# Revit family: 15-42-0035-DN040-400
name_source: partatom
category: Pipe Accessories
units: mm (PartAtom-declared; Revit-internal decimal feet)

## family parameters
Always vertical = No
Cut with Voids When Loaded = No
Part Type = Valve - Breaks Into
Round Connector Dimension = Use Diameter
Shared = No
Work Plane-Based = No

## types (12) — shared parameters
Body_Wallthickness = 15 mm  [stored 0.0492126 ft]
DN 050 = Yes
DN040_PN10/16 = 15-040-40-016
DN050_PN10/16 = 15-050-40-016
DN065_PN10/16 = 15-065-42-016
DN080_PN10/16 = 15-080-42-01464099
DN100_PN10/16 = 15-100-42-01464099
DN125_PN10/16 = 15-125-42-01464099
DN150_PN10/16 = 15-150-42-01464099
DN200_PN10 = 15-200-42-00464099
DN200_PN16 = 15-200-42-01464099
DN250_PN10 = 15-250-42-006
DN250_PN16 = 15-250-42-016
DN300_PN10 = 15-300-42-006
DN300_PN16 = 15-300-42-016
DN350_PN10 = 15-350-40-006
DN350_PN16 = 15-350-40-016
DN400_PN10 = 15-400-40-006
Ftc = 4 mm  [stored 0.0131234 ft]
Name_Height_reference = 10 mm  [stored 0.0328084 ft]
Rib_Thickness = 18 mm  [stored 0.0590551 ft]
Search_table = 15-42-0035-DN040-400
zero-valued in all types: Bottom_Reference

## per-type parameters (varying)
- DN 040: At=46 mm  [stored 0.150919 ft]; Body_Height=101 mm; Body_depth=92 mm; Body_width=74 mm; Bonnet_Flange_Depth=118 mm; Bonnet_Flange_Width=68 mm; Bonnet_Flange_cut=8 mm  [stored 0.0262467 ft]; Bonnet_Flange_thickness=15 mm  [stored 0.0492126 ft]; Bonnet_Height=38 mm  [stored 0.124672 ft]; Bonnet_Reference_height=91 mm; Bonnet_Thickness=75 mm; Bt=75 mm; Bt_2=68 mm; CL _Thickness=26 mm; CL_Height=51 mm; Cut_Reference=280 mm; D=63 mm; D1=10 mm  [stored 0.0328084 ft]; D2=39 mm  [stored 0.127953 ft]; DN 040=Yes; DN 065=Yes; DN 080=Yes; DN 100=Yes; DN 125=Yes; DN 150=Yes; DN 200=Yes; DN 250=Yes; DN 300=Yes; DN 350=Yes; DN 400=Yes; DN400_PN16=15-400-40-016; Description_=AVK_GATE_VALVE,FLANGED; E=14 mm  [stored 0.0459318 ft]; F1=16 mm  [stored 0.0524934 ft]; Fillet_Thickness=6 mm  [stored 0.019685 ft]; Flange_OR=75 mm; Flange_Thickness=19 mm  [stored 0.062336 ft]; Flange_Thickness_cut=28 mm  [stored 0.0918635 ft]; Ftc_reference_height=75 mm; H=241 mm; H1=202 mm; H3=277 mm; Horizontal_Flange_width=72 mm; ID (Radius)=20 mm  [stored 0.0656168 ft]; L=140 mm; L_Dia=40 mm  [stored 0.131234 ft]; Name_Reference=67 mm; Name_Width=37 mm  [stored 0.121391 ft]; Neck_H=37 mm  [stored 0.121391 ft]; Neck_T=24 mm  [stored 0.0787402 ft]; Neck_T2=22 mm  [stored 0.0721785 ft]; Nominal Diameter (DN)=40 mm  [stored 0.131234 ft]; R1tv=750 mm; R2f=15 mm  [stored 0.0492126 ft]; RF_Dia=42 mm  [stored 0.137795 ft]; Rf=120 mm; Rib_Height_Reference_1=120 mm; Rib_Height_Reference_2=110 mm; Rib_Height_Reference_3=100 mm; Rib_Height_Reference_4=40 mm  [stored 0.131234 ft]; Rib_Width_1=37 mm  [stored 0.121391 ft]; Rib_Width_2=37 mm  [stored 0.121391 ft]; Rib_Width_3=37 mm  [stored 0.121391 ft]; Rib_depth_1=37 mm  [stored 0.121391 ft]; Rib_depth_2=37 mm  [stored 0.121391 ft]; Rib_depth_3=37 mm  [stored 0.121391 ft]; Rt=250 mm; URL product pages=https://www.avkvalves.com
- DN 050: At=45 mm  [stored 0.147638 ft]; Body_Height=101 mm; Body_depth=90 mm; Body_width=72 mm; Bonnet_Flange_Depth=118 mm; Bonnet_Flange_Width=82 mm; Bonnet_Flange_cut=8 mm  [stored 0.0262467 ft]; Bonnet_Flange_thickness=15 mm  [stored 0.0492126 ft]; Bonnet_Height=41 mm; Bonnet_Reference_height=91 mm; Bonnet_Thickness=73 mm; Bt=73 mm; Bt_2=66 mm; CL _Thickness=25 mm  [stored 0.082021 ft]; CL_Height=50 mm; Cut_Reference=300 mm; D=63 mm; D1=10 mm  [stored 0.0328084 ft]; D2=39 mm  [stored 0.127953 ft]; DN 040=No; DN 065=No; DN 080=No; DN 100=No; DN 125=No; DN 150=No; DN 200=No; DN 250=No; DN 300=No; DN 350=No; DN 400=No; DN400_PN16=15-400-40-016; Description_=AVK_GATE_VALVE,FLANGED; E=11 mm  [stored 0.0360892 ft]; F1=16 mm  [stored 0.0524934 ft]; Fillet_Thickness=6 mm  [stored 0.019685 ft]; Flange_OR=83 mm; Flange_Thickness=19 mm  [stored 0.062336 ft]; Flange_Thickness_cut=29 mm  [stored 0.0951444 ft]; Ftc_reference_height=83 mm; H=241 mm; H1=202 mm; H3=324 mm; Horizontal_Flange_width=166 mm; ID (Radius)=25 mm  [stored 0.082021 ft]; L=150 mm; L_Dia=50 mm; Name_Reference=71 mm; Name_Width=36 mm  [stored 0.11811 ft]; Neck_H=41 mm; Neck_T=23 mm  [stored 0.0754593 ft]; Neck_T2=21 mm; Nominal Diameter (DN)=50 mm; R1tv=825 mm; R2f=15 mm  [stored 0.0492126 ft]; RF_Dia=50 mm; Rf=277 mm; Rib_Height_Reference_1=120 mm; Rib_Height_Reference_2=110 mm; Rib_Height_Reference_3=100 mm; Rib_Height_Reference_4=60 mm; Rib_Width_1=36 mm  [stored 0.11811 ft]; Rib_Width_2=36 mm  [stored 0.11811 ft]; Rib_Width_3=36 mm  [stored 0.11811 ft]; Rib_depth_1=36 mm  [stored 0.11811 ft]; Rib_depth_2=36 mm  [stored 0.11811 ft]; Rib_depth_3=36 mm  [stored 0.11811 ft]; Rt=275 mm; URL product pages=https://www.avkvalves.com
- DN 065: At=54 mm; Body_Height=115 mm; Body_depth=107 mm; Body_width=72 mm; Bonnet_Flange_Depth=135 mm; Bonnet_Flange_Width=65 mm; Bonnet_Flange_cut=8 mm  [stored 0.0262467 ft]; Bonnet_Flange_thickness=15 mm  [stored 0.0492126 ft]; Bonnet_Height=47 mm  [stored 0.154199 ft]; Bonnet_Reference_height=105 mm; Bonnet_Thickness=73 mm; Bt=73 mm; Bt_2=66 mm; CL _Thickness=25 mm  [stored 0.082021 ft]; CL_Height=59 mm; Cut_Reference=340 mm; D=63 mm; D1=10 mm  [stored 0.0328084 ft]; D2=51 mm; DN 040=Yes; DN 065=Yes; DN 080=Yes; DN 100=Yes; DN 125=Yes; DN 150=Yes; DN 200=Yes; DN 250=Yes; DN 300=Yes; DN 350=Yes; DN 400=Yes; DN400_PN16=15-400-40-016; Description_=AVK_GATE-VALVE,FLANGED; E=11 mm  [stored 0.0360892 ft]; F1=20 mm  [stored 0.0656168 ft]; Fillet_Thickness=6 mm  [stored 0.019685 ft]; Flange_OR=93 mm; Flange_Thickness=19 mm  [stored 0.062336 ft]; Flange_Thickness_cut=30 mm  [stored 0.0984252 ft]; Ftc_reference_height=93 mm; H=278 mm; H1=227 mm; H3=371 mm; Horizontal_Flange_width=186 mm; ID (Radius)=33 mm  [stored 0.108268 ft]; L=170 mm; L_Dia=65 mm; Name_Reference=96 mm; Name_Width=36 mm  [stored 0.11811 ft]; Neck_H=43 mm; Neck_T=23 mm  [stored 0.0754593 ft]; Neck_T2=21 mm; Nominal Diameter (DN)=65 mm; R1tv=930 mm; R2f=15 mm  [stored 0.0492126 ft]; RF_Dia=59 mm; Rf=310 mm; Rib_Height_Reference_1=120 mm; Rib_Height_Reference_2=110 mm; Rib_Height_Reference_3=100 mm; Rib_Height_Reference_4=75 mm; Rib_Width_1=36 mm  [stored 0.11811 ft]; Rib_Width_2=36 mm  [stored 0.11811 ft]; Rib_Width_3=36 mm  [stored 0.11811 ft]; Rib_depth_1=36 mm  [stored 0.11811 ft]; Rib_depth_2=36 mm  [stored 0.11811 ft]; Rib_depth_3=36 mm  [stored 0.11811 ft]; Rt=310 mm; URL product pages=https://www.avkvalves.com
- DN 080: At=70 mm; Body_Height=108 mm; Body_depth=140 mm; Body_width=75 mm; Bonnet_Flange_Depth=171 mm; Bonnet_Flange_Width=76 mm; Bonnet_Flange_cut=8 mm  [stored 0.0262467 ft]; Bonnet_Flange_thickness=15 mm  [stored 0.0492126 ft]; Bonnet_Height=50 mm; Bonnet_Reference_height=98 mm; Bonnet_Thickness=77 mm; Bt=77 mm; Bt_2=69 mm; CL _Thickness=27 mm  [stored 0.0885827 ft]; CL_Height=75 mm; Cut_Reference=360 mm; D=63 mm; D1=10 mm  [stored 0.0328084 ft]; D2=37 mm  [stored 0.121391 ft]; DN 040=Yes; DN 065=Yes; DN 080=Yes; DN 100=Yes; DN 125=Yes; DN 150=Yes; DN 200=Yes; DN 250=Yes; DN 300=Yes; DN 350=Yes; DN 400=Yes; DN400_PN16=15-400-40-016; Description_=AVK_GATE_VALVE,FLANGED; E=15 mm  [stored 0.0492126 ft]; F1=20 mm  [stored 0.0656168 ft]; Fillet_Thickness=6 mm  [stored 0.019685 ft]; Flange_OR=100 mm; Flange_Thickness=19 mm  [stored 0.062336 ft]; Flange_Thickness_cut=30 mm  [stored 0.0984252 ft]; Ftc_reference_height=100 mm; H=284 mm; H1=247 mm; H3=384 mm; Horizontal_Flange_width=200 mm; ID (Radius)=40 mm  [stored 0.131234 ft]; L=180 mm; L_Dia=80 mm; Name_Reference=90 mm; Name_Width=38 mm  [stored 0.124672 ft]; Neck_H=49 mm; Neck_T=25 mm  [stored 0.082021 ft]; Neck_T2=23 mm  [stored 0.0754593 ft]; Nominal Diameter (DN)=80 mm; R1tv=1000 mm; R2f=15 mm  [stored 0.0492126 ft]; RF_Dia=66 mm; Rf=333 mm; Rib_Height_Reference_1=120 mm; Rib_Height_Reference_2=110 mm; Rib_Height_Reference_3=100 mm; Rib_Height_Reference_4=85 mm; Rib_Width_1=38 mm  [stored 0.124672 ft]; Rib_Width_2=38 mm  [stored 0.124672 ft]; Rib_Width_3=38 mm  [stored 0.124672 ft]; Rib_depth_1=38 mm  [stored 0.124672 ft]; Rib_depth_2=38 mm  [stored 0.124672 ft]; Rib_depth_3=38 mm  [stored 0.124672 ft]; Rt=333 mm; URL product pages=https://www.avkvalves.com
- DN 100: At=83 mm; Body_Height=122 mm; Body_depth=166 mm; Body_width=80 mm; Bonnet_Flange_Depth=192 mm; Bonnet_Flange_Width=81 mm; Bonnet_Flange_cut=8 mm  [stored 0.0262467 ft]; Bonnet_Flange_thickness=15 mm  [stored 0.0492126 ft]; Bonnet_Height=55 mm; Bonnet_Reference_height=112 mm; Bonnet_Thickness=82 mm; Bt=82 mm; Bt_2=74 mm; CL _Thickness=29 mm  [stored 0.0951444 ft]; CL_Height=88 mm; Cut_Reference=380 mm; D=63 mm; D1=10 mm  [stored 0.0328084 ft]; D2=41 mm; DN 040=Yes; DN 065=Yes; DN 080=Yes; DN 100=Yes; DN 125=Yes; DN 150=Yes; DN 200=Yes; DN 250=Yes; DN 300=Yes; DN 350=Yes; DN 400=Yes; DN400_PN16=15-400-40-016; Description_=AVK_GATE_VALVE,FLANGED; E=15 mm  [stored 0.0492126 ft]; F1=22 mm  [stored 0.0721785 ft]; Fillet_Thickness=6 mm  [stored 0.019685 ft]; Flange_OR=110 mm; Flange_Thickness=19 mm  [stored 0.062336 ft]; Flange_Thickness_cut=30 mm  [stored 0.0984252 ft]; Ftc_reference_height=110 mm; H=311 mm; H1=270 mm; H3=421 mm; Horizontal_Flange_width=220 mm; ID (Radius)=50 mm; L=190 mm; L_Dia=100 mm; Name_Reference=101 mm; Name_Width=40 mm  [stored 0.131234 ft]; Neck_H=45 mm  [stored 0.147638 ft]; Neck_T=27 mm  [stored 0.0885827 ft]; Neck_T2=25 mm  [stored 0.082021 ft]; Nominal Diameter (DN)=100 mm; R1tv=1100 mm; R2f=15 mm  [stored 0.0492126 ft]; RF_Dia=78 mm; Rf=367 mm; Rib_Height_Reference_1=120 mm; Rib_Height_Reference_2=110 mm; Rib_Height_Reference_3=100 mm; Rib_Height_Reference_4=90 mm; Rib_Width_1=40 mm  [stored 0.131234 ft]; Rib_Width_2=40 mm  [stored 0.131234 ft]; Rib_Width_3=40 mm  [stored 0.131234 ft]; Rib_depth_1=40 mm  [stored 0.131234 ft]; Rib_depth_2=40 mm  [stored 0.131234 ft]; Rib_depth_3=40 mm  [stored 0.131234 ft]; Rt=367 mm; URL product pages=https://www.avkvalves.com
- DN 150: At=121 mm; Body_Height=172 mm; Body_depth=242 mm; Body_width=95 mm; Bonnet_Flange_Depth=272 mm; Bonnet_Flange_Width=116 mm; Bonnet_Flange_cut=8 mm  [stored 0.0262467 ft]; Bonnet_Flange_thickness=15 mm  [stored 0.0492126 ft]; Bonnet_Height=71 mm; Bonnet_Reference_height=162 mm; Bonnet_Thickness=97 mm; Bt=97 mm; Bt_2=89 mm; CL _Thickness=34 mm  [stored 0.111549 ft]; CL_Height=126 mm; Cut_Reference=420 mm; D=63 mm; D1=10 mm  [stored 0.0328084 ft]; D2=43 mm; DN 040=Yes; DN 065=Yes; DN 080=Yes; DN 100=Yes; DN 125=Yes; DN 150=Yes; DN 200=Yes; DN 250=Yes; DN 300=Yes; DN 350=Yes; DN 400=Yes; DN400_PN16=15-400-40-016
15-400-40-016
15-400-40-016
15-400-40-016
15-400-40-016; Description_=AVK_GATE_VALVE,FLANGED; E=15 mm  [stored 0.0492126 ft]; F1=22 mm  [stored 0.0721785 ft]; Fillet_Thickness=12 mm  [stored 0.0393701 ft]; Flange_OR=142 mm; Flange_Thickness=19 mm  [stored 0.062336 ft]; Flange_Thickness_cut=34 mm  [stored 0.111549 ft]; Ftc_reference_height=142 mm; H=408 mm; H1=365 mm; H3=550 mm; Horizontal_Flange_width=284 mm; ID (Radius)=75 mm; L=210 mm; L_Dia=150 mm; Name_Reference=143 mm; Name_Width=48 mm; Neck_H=52 mm; Neck_T=32 mm  [stored 0.104987 ft]; Neck_T2=30 mm  [stored 0.0984252 ft]; Nominal Diameter (DN)=150 mm; R1tv=1420 mm; R2f=30 mm  [stored 0.0984252 ft]; RF_Dia=106 mm; Rf=473 mm; Rib_Height_Reference_1=120 mm; Rib_Height_Reference_2=110 mm; Rib_Height_Reference_3=100 mm; Rib_Height_Reference_4=150 mm; Rib_Width_1=48 mm; Rib_Width_2=48 mm; Rib_Width_3=48 mm; Rib_depth_1=48 mm; Rib_depth_2=48 mm; Rib_depth_3=48 mm; Rt=473 mm; URL product pages=https://www.avkvalves.com
- DN 200: At=147 mm; Body_Height=220 mm; Body_depth=294 mm; Body_width=108 mm; Bonnet_Flange_Depth=332 mm; Bonnet_Flange_Width=132 mm; Bonnet_Flange_cut=13 mm; Bonnet_Flange_thickness=25 mm  [stored 0.082021 ft]; Bonnet_Height=85 mm; Bonnet_Reference_height=210 mm; Bonnet_Thickness=110 mm; Bt=110 mm; Bt_2=102 mm; CL _Thickness=34 mm  [stored 0.111549 ft]; CL_Height=152 mm; Cut_Reference=460 mm; D=63 mm; D1=10 mm  [stored 0.0328084 ft]; D2=51 mm; DN 040=Yes; DN 065=Yes; DN 080=Yes; DN 100=Yes; DN 125=Yes; DN 150=Yes; DN 200=Yes; DN 250=Yes; DN 300=Yes; DN 350=Yes; DN 400=Yes; DN400_PN16=15-400-40-016; Description_=AVK_GATE_VALVE,FLANGED; E=15 mm  [stored 0.0492126 ft]; F1=28 mm  [stored 0.0918635 ft]; Fillet_Thickness=24 mm  [stored 0.0787402 ft]; Flange_OR=170 mm; Flange_Thickness=20 mm  [stored 0.0656168 ft]; Flange_Thickness_cut=35 mm  [stored 0.114829 ft]; Ftc_reference_height=170 mm; H=507 mm; H1=456 mm; H3=677 mm; Horizontal_Flange_width=340 mm; ID (Radius)=100 mm; L=230 mm; L_Dia=200 mm; Name_Reference=183 mm; Name_Width=54 mm; Neck_H=69 mm; Neck_T=32 mm  [stored 0.104987 ft]; Neck_T2=30 mm  [stored 0.0984252 ft]; Nominal Diameter (DN)=200 mm; R1tv=1700 mm; R2f=60 mm; RF_Dia=133 mm; Rf=567 mm; Rib_Height_Reference_1=120 mm; Rib_Height_Reference_2=110 mm; Rib_Height_Reference_3=100 mm; Rib_Height_Reference_4=180 mm; Rib_Width_1=54 mm; Rib_Width_2=54 mm; Rib_Width_3=54 mm; Rib_depth_1=54 mm; Rib_depth_2=54 mm; Rib_depth_3=54 mm; Rt=567 mm; URL product pages=https://www.avkvalves.com
https://www.avkvalves.com
- DN 250: At=171 mm; Body_Height=305 mm; Body_depth=342 mm; Body_width=124 mm; Bonnet_Flange_Depth=372 mm; Bonnet_Flange_Width=158 mm; Bonnet_Flange_cut=13 mm; Bonnet_Flange_thickness=25 mm  [stored 0.082021 ft]; Bonnet_Height=100 mm; Bonnet_Reference_height=295 mm; Bonnet_Thickness=126 mm; Bt=126 mm; Bt_2=118 mm; CL _Thickness=42 mm  [stored 0.137795 ft]; CL_Height=176 mm; Cut_Reference=500 mm; D=88 mm; D1=15 mm  [stored 0.0492126 ft]; D2=62 mm; DN 040=Yes; DN 065=Yes; DN 080=Yes; DN 100=Yes; DN 125=Yes; DN 150=Yes; DN 200=Yes; DN 250=Yes; DN 300=Yes; DN 350=Yes; DN 400=Yes; DN400_PN16=15-400-40-016; Description_=AVK_GATE_VALVE,FLANGED; E=13 mm; F1=27 mm  [stored 0.0885827 ft]; Fillet_Thickness=24 mm  [stored 0.0787402 ft]; Flange_OR=200 mm; Flange_Thickness=22 mm  [stored 0.0721785 ft]; Flange_Thickness_cut=38 mm  [stored 0.124672 ft]; Ftc_reference_height=200 mm; H=617 mm; H1=555 mm; H3=817 mm; Horizontal_Flange_width=400 mm; ID (Radius)=125 mm; L=250 mm; L_Dia=250 mm; Name_Reference=270 mm; Name_Width=62 mm; Neck_H=61 mm; Neck_T=40 mm  [stored 0.131234 ft]; Neck_T2=38 mm  [stored 0.124672 ft]; Nominal Diameter (DN)=250 mm; R1tv=2000 mm; R2f=60 mm; RF_Dia=160 mm; Rf=667 mm; Rib_Height_Reference_1=90 mm; Rib_Height_Reference_2=110 mm; Rib_Height_Reference_3=100 mm; Rib_Height_Reference_4=200 mm; Rib_Width_1=140 mm; Rib_Width_2=140 mm; Rib_Width_3=62 mm; Rib_depth_1=372 mm; Rib_depth_2=62 mm; Rib_depth_3=62 mm; Rt=667 mm; URL product pages=https://www.avkvalves.com
- DN 300: At=209 mm; Body_Height=370 mm; Body_depth=418 mm; Body_width=157 mm; Bonnet_Flange_Depth=432 mm; Bonnet_Flange_Width=206 mm; Bonnet_Flange_cut=18 mm  [stored 0.0590551 ft]; Bonnet_Flange_thickness=35 mm  [stored 0.114829 ft]; Bonnet_Height=114 mm; Bonnet_Reference_height=360 mm; Bonnet_Thickness=160 mm; Bt=160 mm; Bt_2=151 mm; CL _Thickness=59 mm; CL_Height=214 mm; Cut_Reference=540 mm; D=88 mm; D1=15 mm  [stored 0.0492126 ft]; D2=61 mm; DN 040=Yes; DN 065=Yes; DN 080=Yes; DN 100=Yes; DN 125=Yes; DN 150=Yes; DN 200=Yes; DN 250=Yes; DN 300=Yes; DN 350=Yes; DN 400=Yes; DN400_PN16=15-400-40-016; Description_=AVK_GATE_VALVE,FLANGED; E=13 mm; F1=27 mm  [stored 0.0885827 ft]; Fillet_Thickness=24 mm  [stored 0.0787402 ft]; Flange_OR=228 mm; Flange_Thickness=25 mm  [stored 0.082021 ft]; Flange_Thickness_cut=39 mm  [stored 0.127953 ft]; Ftc_reference_height=228 mm; H=691 mm; H1=630 mm; H3=919 mm; Horizontal_Flange_width=456 mm; ID (Radius)=150 mm; L=270 mm; L_Dia=300 mm; Name_Reference=250 mm; Name_Width=79 mm; Neck_H=33 mm  [stored 0.108268 ft]; Neck_T=57 mm; Neck_T2=55 mm; Nominal Diameter (DN)=300 mm; R1tv=2280 mm; R2f=60 mm; RF_Dia=185 mm; Rf=760 mm; Rib_Height_Reference_1=178 mm; Rib_Height_Reference_2=285 mm; Rib_Height_Reference_3=150 mm; Rib_Height_Reference_4=300 mm; Rib_Width_1=168 mm; Rib_Width_2=168 mm; Rib_Width_3=79 mm; Rib_depth_1=432 mm; Rib_depth_2=432 mm; Rib_depth_3=79 mm; Rt=760 mm; URL product pages=https://www.avkvalves.com
- DN 350: At=250 mm; Body_Height=485 mm; Body_depth=500 mm; Body_width=170 mm; Bonnet_Flange_Depth=554 mm; Bonnet_Flange_Width=180 mm; Bonnet_Flange_cut=18 mm  [stored 0.0590551 ft]; Bonnet_Flange_thickness=35 mm  [stored 0.114829 ft]; Bonnet_Height=130 mm; Bonnet_Reference_height=475 mm; Bonnet_Thickness=173 mm; Bt=173 mm; Bt_2=164 mm; CL _Thickness=65 mm; CL_Height=255 mm; Cut_Reference=580 mm; D=110 mm; D1=15 mm  [stored 0.0492126 ft]; D2=107 mm; DN 040=Yes; DN 065=Yes; DN 080=Yes; DN 100=Yes; DN 125=Yes; DN 150=Yes; DN 200=Yes; DN 250=Yes; DN 300=Yes; DN 350=Yes; DN 400=Yes; DN400_PN16=15-400-40-016; Description_=AVK_GATE_VALVE,FLANGED; E=28 mm  [stored 0.0918635 ft]; F1=37 mm  [stored 0.121391 ft]; Fillet_Thickness=24 mm  [stored 0.0787402 ft]; Flange_OR=260 mm; Flange_Thickness=27 mm  [stored 0.0885827 ft]; Flange_Thickness_cut=43 mm; Ftc_reference_height=260 mm; H=907 mm; H1=800 mm; H3=1221 mm; Horizontal_Flange_width=628 mm; ID (Radius)=175 mm; L=290 mm; L_Dia=350 mm; Name_Reference=404 mm; Name_Width=85 mm; Neck_H=32 mm  [stored 0.104987 ft]; Neck_T=63 mm; Neck_T2=61 mm; Nominal Diameter (DN)=350 mm; R1tv=2600 mm; R2f=60 mm; RF_Dia=215 mm; Rf=1047 mm; Rib_Height_Reference_1=70 mm; Rib_Height_Reference_2=185 mm; Rib_Height_Reference_3=305 mm; Rib_Height_Reference_4=410 mm; Rib_Width_1=190 mm; Rib_Width_2=190 mm; Rib_Width_3=190 mm; Rib_depth_1=560 mm; Rib_depth_2=560 mm; Rib_depth_3=560 mm; Rt=867 mm; URL product pages=https://www.avkvalves.com
- DN 400: At=260 mm; Body_Height=512 mm; Body_depth=520 mm; Body_width=200 mm; Bonnet_Flange_Depth=554 mm; Bonnet_Flange_Width=194 mm; Bonnet_Flange_cut=35 mm  [stored 0.114829 ft]; Bonnet_Flange_thickness=70 mm; Bonnet_Height=145 mm; Bonnet_Reference_height=502 mm; Bonnet_Thickness=204 mm; Bt=204 mm; Bt_2=194 mm; CL _Thickness=76 mm; CL_Height=265 mm; Cut_Reference=620 mm; D=110 mm; D1=15 mm  [stored 0.0492126 ft]; D2=91 mm; DN 040=Yes; DN 065=Yes; DN 080=Yes; DN 100=Yes; DN 125=Yes; DN 150=Yes; DN 200=Yes; DN 250=Yes; DN 300=Yes; DN 350=Yes; DN 400=Yes; DN400_PN16=15-400-40-016; Description_=AVK_GATE_VALVE,FLANGED; E=28 mm  [stored 0.0918635 ft]; F1=37 mm  [stored 0.121391 ft]; Fillet_Thickness=32 mm  [stored 0.104987 ft]; Flange_OR=290 mm; Flange_Thickness=28 mm  [stored 0.0918635 ft]; Flange_Thickness_cut=45 mm  [stored 0.147638 ft]; Ftc_reference_height=290 mm; H=951 mm; H1=860 mm; H3=1239 mm; Horizontal_Flange_width=576 mm; ID (Radius)=200 mm; L=310 mm; L_Dia=400 mm; Name_Reference=426 mm; Name_Width=100 mm; Neck_H=55 mm; Neck_T=74 mm; Neck_T2=72 mm; Nominal Diameter (DN)=400 mm; R1tv=2900 mm; R2f=80 mm; RF_Dia=240 mm; Rf=960 mm; Rib_Height_Reference_1=81 mm; Rib_Height_Reference_2=210 mm; Rib_Height_Reference_3=330 mm; Rib_Height_Reference_4=440 mm; Rib_Width_1=248 mm; Rib_Width_2=248 mm; Rib_Width_3=248 mm; Rib_depth_1=564 mm; Rib_depth_2=564 mm; Rib_depth_3=564 mm; Rt=967 mm; URL product pages=https://www.avkvalves.com
- DN 125: At=97 mm; Body_Height=137 mm; Body_depth=194 mm; Body_width=90 mm; Bonnet_Flange_Depth=220 mm; Bonnet_Flange_Width=83 mm; Bonnet_Flange_cut=8 mm  [stored 0.0262467 ft]; Bonnet_Flange_thickness=15 mm  [stored 0.0492126 ft]; Bonnet_Height=63 mm; Bonnet_Reference_height=127 mm; Bonnet_Thickness=92 mm; Bt=92 mm; Bt_2=84 mm; CL _Thickness=34 mm  [stored 0.111549 ft]; CL_Height=102 mm; Cut_Reference=400 mm; D=63 mm; D1=10 mm  [stored 0.0328084 ft]; D2=41 mm; DN 040=Yes; DN 065=Yes; DN 080=Yes; DN 100=Yes; DN 125=Yes; DN 150=Yes; DN 200=Yes; DN 250=Yes; DN 300=Yes; DN 350=Yes; DN 400=Yes; DN400_PN16=15-400-40-016; Description_=AVK_GATE_VALVE,FLANGED; E=15 mm  [stored 0.0492126 ft]; F1=22 mm  [stored 0.0721785 ft]; Fillet_Thickness=6 mm  [stored 0.019685 ft]; Flange_OR=125 mm; Flange_Thickness=19 mm  [stored 0.062336 ft]; Flange_Thickness_cut=31 mm; Ftc_reference_height=125 mm; H=352 mm; H1=311 mm; H3=477 mm; Horizontal_Flange_width=250 mm; ID (Radius)=63 mm; L=200 mm; L_Dia=125 mm; Name_Reference=114 mm; Name_Width=45 mm  [stored 0.147638 ft]; Neck_H=57 mm; Neck_T=32 mm  [stored 0.104987 ft]; Neck_T2=30 mm  [stored 0.0984252 ft]; Nominal Diameter (DN)=125 mm; R1tv=1250 mm; R2f=15 mm  [stored 0.0492126 ft]; RF_Dia=92 mm; Rf=417 mm; Rib_Height_Reference_1=120 mm; Rib_Height_Reference_2=110 mm; Rib_Height_Reference_3=100 mm; Rib_Height_Reference_4=120 mm; Rib_Width_1=45 mm  [stored 0.147638 ft]; Rib_Width_2=45 mm  [stored 0.147638 ft]; Rib_Width_3=45 mm  [stored 0.147638 ft]; Rib_depth_1=45 mm  [stored 0.147638 ft]; Rib_depth_2=45 mm  [stored 0.147638 ft]; Rib_depth_3=45 mm  [stored 0.147638 ft]; Rt=417 mm; URL product pages=https://www.avkvalves.com

note: [stored X ft] marks values corroborated as IEEE doubles in the binary element streams (Revit-internal decimal feet)

## geometry (parser evidence)
native form markers: Sweep x3
no freeform markers — native parametric forms only
